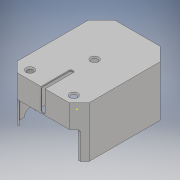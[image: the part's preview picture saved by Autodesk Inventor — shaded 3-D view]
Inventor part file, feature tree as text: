
AUTODESK INVENTOR PART (.ipt)
format: ipt  version: 2017 (Build 210142000, 142)  size: 278,016 bytes
history: native  units: mm
features: sketch x11, extrude x10, other x6, fillet x4, hole x3, projected_geometry x2
ambient origin geometry x8: Origin, YZ Plane, XZ Plane, XY Plane, X Axis, Y Axis, Z Axis, Center Point
bodies: Body1 (feature_tree)
feature tree (36):
  other  "Твердое тело1"
  sketch  "Эскиз1"
  extrude  "Выдавливание1"  Depth=60.0mm
  extrude  "Выдавливание2"  Depth=80.0mm
  fillet  "Сопряжение1"  Radius=11.0mm
  extrude  "Выдавливание3"  Depth=11.0mm
  extrude  "Выдавливание4"  Depth=8.5mm
  extrude  "Выдавливание5"  Depth=8.5mm
  other  "Комбинировать1"
  hole  "Отверстие4"  [1 undecoded]
  hole  "Отверстие5"  [1 undecoded]
  hole  "Отверстие6"  [1 undecoded]
  fillet  "Сопряжение2"  Radius=11.0mm
  fillet  "Сопряжение3"  Radius=1.2mm
  extrude  "Выдавливание6"  Depth=1.0mm TaperAngle=0.0deg
  extrude  "Выдавливание7"  Depth=43.0mm TaperAngle=0.0deg
  extrude  "Выдавливание8"  Depth=1.0mm
  other  "Комбинировать2"
  fillet  "Сопряжение4"  Radius=3.5mm
  sketch  "Эскиз8"
  sketch  "Эскиз9"
  sketch  "Эскиз10"
  extrude  "Выдавливание10"  Depth=25.0mm
  other  "РабПлоскость2"
  extrude  "Выдавливание12"  Depth=18.0mm TaperAngle=0.0deg
  other  "Твердое тело2"
  sketch  "Эскиз2"
  sketch  "Эскиз3"
  sketch  "Эскиз4"
  other  "Твердое тело3"
  sketch  "Эскиз5"
  sketch  "Эскиз6"
  sketch  "Эскиз11"
  projected_geometry  "Спроецированная петля1"
  sketch  "Эскиз13"
  projected_geometry  "Спроецированная петля2"
note: 3 required parameter values undecoded (feature->parameter linkage not recoverable at this tier; creation-order binding heuristic only, values carry confidence <= 0.55)
